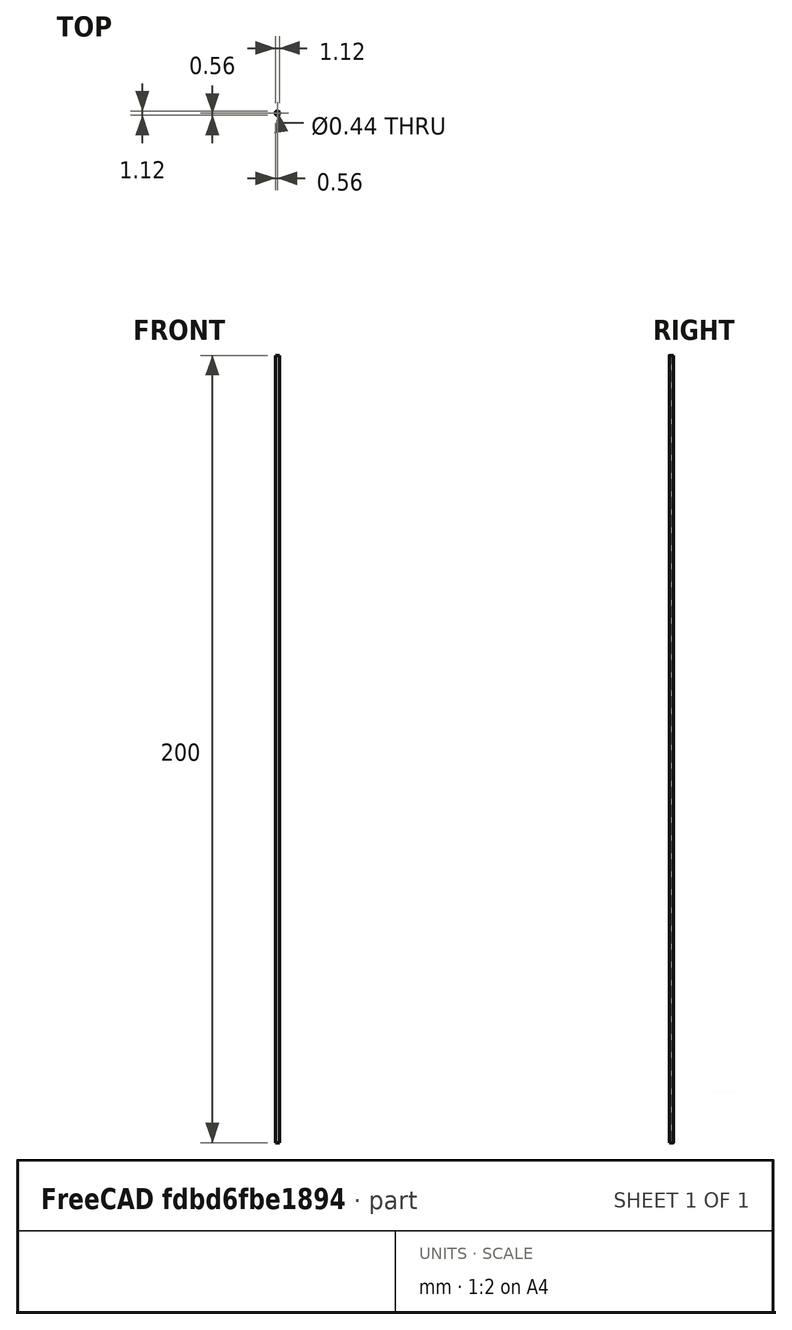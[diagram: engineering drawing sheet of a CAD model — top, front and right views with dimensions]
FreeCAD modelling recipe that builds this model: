
FCSTD DOCUMENT  (FreeCAD 0.20R29603 (Git))
Label: CableCase
License: All rights reserved
LicenseURL: http://en.wikipedia.org/wiki/All_rights_reserved
objects: PartDesign::AdditiveCylinder×1, Sketcher::SketchObject×1, PartDesign::Pocket×1, PartDesign::Body×1
note: 6 computed .brp shape members not serialized (recipe doc carries the construction recipe); baked Part::Feature solids carry a one-line shape summary decoded from their .brp

FEATURE [PartDesign::AdditiveCylinder] Cylinder
  Angle = 360
  AttacherType = Attacher::AttachEngine3D
  FirstAngle = 0
  Height = 200
  MapMode = 5
  Radius = 0.56
  Refine = true
  SecondAngle = 0
  Support = -> [XY_Plane]
FEATURE [Sketcher::SketchObject] Sketch
  FullyConstrained = true
  MapMode = 5
  Placement = pos=(0,0,200) rot=(0,0,1;0rad)
  Support = -> [Cylinder]
  sketch-geometry (1):
    g0: Circle CenterX=0 CenterY=0 CenterZ=0 NormalX=0 NormalY=0 NormalZ=1 AngleXU=0 Radius=0.218838
  constraints (2):
    c: Coincident(g0,g-1)
    c: Diameter(g0) = 0.437676
FEATURE [PartDesign::Pocket] Pocket
  BaseFeature = -> Cylinder
  Direction = (0,0,-1)
  Length = 5
  Length2 = 5
  Profile = -> Sketch
  ReferenceAxis = -> Sketch [N_Axis]
  Refine = true
  Type = 1
FEATURE [PartDesign::Body] Body
  Group = -> [Cylinder,Sketch,Pocket]
  Origin = -> Origin
  Tip = -> Pocket
